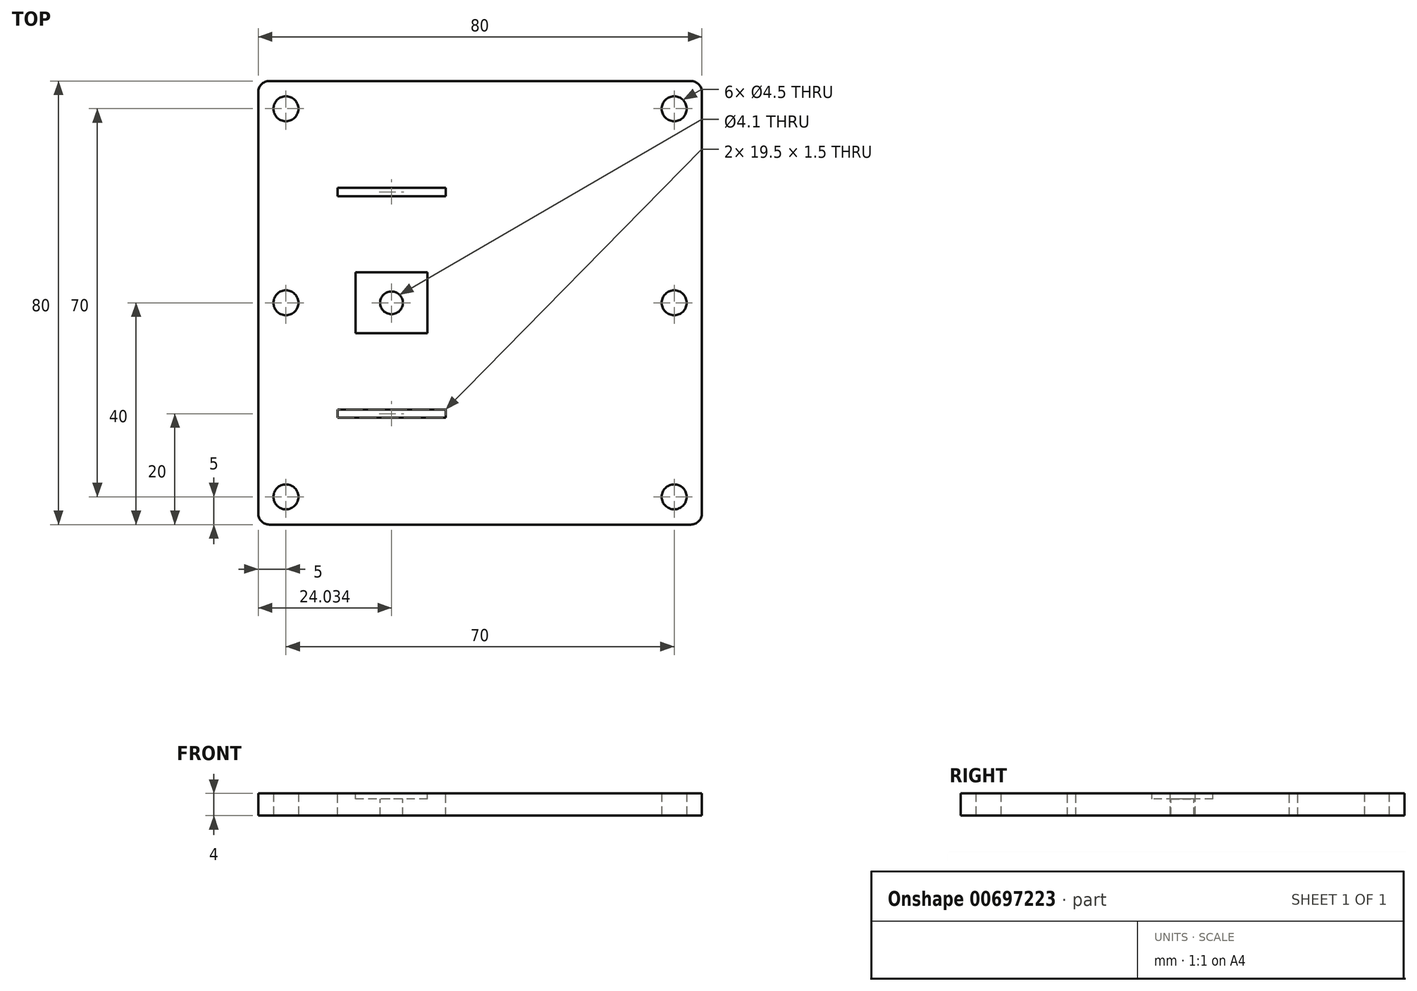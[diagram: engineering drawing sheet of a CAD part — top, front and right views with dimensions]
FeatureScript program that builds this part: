
annotation { "Feature Type Name" : "Feature", "Feature Type Description" : "" }
export const myFeature = defineFeature(function(context is Context, id is Id, definition is map)
    precondition{}
    {
        {
            var Q0;
            Q0=qCreatedBy(makeId("Top.planeOp"),FACE);
            var sketch = newSketch(context, id + "F0", { "sketchPlane" : qUnion([Q0])});
            skLineSegment(sketch, "E0.bottom", {"start": v(38, 40) * mm, "end": v(-38, 40) * mm});
            skLineSegment(sketch, "E0.top", {"start": v(38, -40) * mm, "end": v(-38, -40) * mm});
            skLineSegment(sketch, "E0.left", {"start": v(40, 38) * mm, "end": v(40, -38) * mm});
            skLineSegment(sketch, "E0.right", {"start": v(-40, 38) * mm, "end": v(-40, -38) * mm});
            skPoint(sketch, "E0.middle", {"position": v(0, 0) * mm});
            skCircle(sketch, "E1", {"center": v(-35, 0) * mm, "radius": 2.25 * mm});
            skCircle(sketch, "E2", {"center": v(35, 0) * mm, "radius": 2.25 * mm});
            skPoint(sketch, "E3.visualSharp", {"position": v(-40, 40) * mm});
            skArc(sketch, "E3.filletArc", {"start": v(-38, 40) * mm, "mid": v(-39.41, 39.41) * mm, "end": v(-40, 38) * mm});
            skPoint(sketch, "E4.visualSharp", {"position": v(-40, -40) * mm});
            skArc(sketch, "E4.filletArc", {"start": v(-40, -38) * mm, "mid": v(-39.41, -39.41) * mm, "end": v(-38, -40) * mm});
            skPoint(sketch, "E5.visualSharp", {"position": v(40, 40) * mm});
            skArc(sketch, "E5.filletArc", {"start": v(40, 38) * mm, "mid": v(39.41, 39.41) * mm, "end": v(38, 40) * mm});
            skPoint(sketch, "E6.visualSharp", {"position": v(40, -40) * mm});
            skArc(sketch, "E6.filletArc", {"start": v(38, -40) * mm, "mid": v(39.41, -39.41) * mm, "end": v(40, -38) * mm});
            skLineSegment(sketch, "E7", {"start": v(-35, 0) * mm, "end": v(-35, 40) * mm, "construction": true});
            skLineSegment(sketch, "E8", {"start": v(-35, 0) * mm, "end": v(-35, -40) * mm, "construction": true});
            skLineSegment(sketch, "E9", {"start": v(35, 0) * mm, "end": v(35, 40) * mm, "construction": true});
            skLineSegment(sketch, "E10", {"start": v(35, 0) * mm, "end": v(35, -40) * mm, "construction": true});
            skCircle(sketch, "E11", {"center": v(-35, 35) * mm, "radius": 2.25 * mm});
            skCircle(sketch, "E12", {"center": v(35, 35) * mm, "radius": 2.25 * mm});
            skCircle(sketch, "E13", {"center": v(-35, -35) * mm, "radius": 2.25 * mm});
            skCircle(sketch, "E14", {"center": v(35, -35) * mm, "radius": 2.25 * mm});
            skSolve(sketch);
        }
        {
            var Q0;
            Q0=makeQuery(id+"F0.imprint","IMPRINT",FACE,{"disambiguationData":[TD([[makeQuery(id+"F0.imprint","IMPRINT",EDGE,{"derivedFrom":sQuery(id+"F0.wireOp",EDGE,"E0.bottom")}),1.0]])]});
            extrude(context, id + "F1", {"entities" : qUnion([Q0]), "depth" : 4 * mm, "offsetDistance" : 25 * mm});
        }
        {
            var Q0;
            Q0=makeQuery(id+"F1.opExtrude","CAP_FACE",FACE,{"disambiguationData":[OSD([sQuery(id+"F0.wireOp",EDGE,"E0.bottom"),sQuery(id+"F0.wireOp",EDGE,"E0.top"),sQuery(id+"F0.wireOp",EDGE,"E0.left"),sQuery(id+"F0.wireOp",EDGE,"E0.right"),sQuery(id+"F0.wireOp",EDGE,"E1"),sQuery(id+"F0.wireOp",EDGE,"E2"),sQuery(id+"F0.wireOp",EDGE,"E3.filletArc"),sQuery(id+"F0.wireOp",EDGE,"E4.filletArc"),sQuery(id+"F0.wireOp",EDGE,"E5.filletArc"),sQuery(id+"F0.wireOp",EDGE,"E6.filletArc")])],"isStart":false});
            var sketch = newSketch(context, id + "F2", { "sketchPlane" : qUnion([Q0])});
            skCircle(sketch, "E15", {"center": v(-15.97, 0) * mm, "radius": 2.05 * mm});
            skSolve(sketch);
        }
        {
            var Q0;
            Q0=makeQuery(id+"F2.imprint","IMPRINT",FACE,{"disambiguationData":[TD([[makeQuery(id+"F2.imprint","IMPRINT",EDGE,{"derivedFrom":sQuery(id+"F2.wireOp",EDGE,"E15")}),1.0]])]});
            extrude(context, id + "F3", {"entities" : qUnion([Q0]), "operationType" : NewBodyOperationType.REMOVE, "oppositeDirection" : true, "depth" : 5 * mm, "offsetDistance" : 25 * mm});
        }
        {
            var Q0;
            Q0=makeQuery(id+"F1.opExtrude","CAP_FACE",FACE,{"disambiguationData":[OSD([sQuery(id+"F0.wireOp",EDGE,"E0.bottom"),sQuery(id+"F0.wireOp",EDGE,"E0.top"),sQuery(id+"F0.wireOp",EDGE,"E0.left"),sQuery(id+"F0.wireOp",EDGE,"E0.right"),sQuery(id+"F0.wireOp",EDGE,"E1"),sQuery(id+"F0.wireOp",EDGE,"E2"),sQuery(id+"F0.wireOp",EDGE,"E3.filletArc"),sQuery(id+"F0.wireOp",EDGE,"E4.filletArc"),sQuery(id+"F0.wireOp",EDGE,"E5.filletArc"),sQuery(id+"F0.wireOp",EDGE,"E6.filletArc")])],"isStart":false});
            var sketch = newSketch(context, id + "F4", { "sketchPlane" : qUnion([Q0])});
            skLineSegment(sketch, "E16.bottom", {"start": v(-9.47, 5.5) * mm, "end": v(-22.47, 5.5) * mm});
            skLineSegment(sketch, "E16.top", {"start": v(-9.47, -5.5) * mm, "end": v(-22.47, -5.5) * mm});
            skLineSegment(sketch, "E16.left", {"start": v(-9.47, 5.5) * mm, "end": v(-9.47, -5.5) * mm});
            skLineSegment(sketch, "E16.right", {"start": v(-22.47, 5.5) * mm, "end": v(-22.47, -5.5) * mm});
            skPoint(sketch, "E16.middle", {"position": v(-15.97, 0) * mm});
            skSolve(sketch);
        }
        {
            var Q0;
            Q0=qSketchRegion(id+"F4",true);
            extrude(context, id + "F5", {"entities" : qUnion([Q0]), "operationType" : NewBodyOperationType.REMOVE, "oppositeDirection" : true, "depth" : 1 * mm, "offsetDistance" : 25 * mm});
        }
        {
            var Q0;
            Q0=makeQuery(id+"F1.opExtrude","CAP_FACE",FACE,{"disambiguationData":[OSD([sQuery(id+"F0.wireOp",EDGE,"E0.bottom"),sQuery(id+"F0.wireOp",EDGE,"E0.top"),sQuery(id+"F0.wireOp",EDGE,"E0.left"),sQuery(id+"F0.wireOp",EDGE,"E0.right"),sQuery(id+"F0.wireOp",EDGE,"E1"),sQuery(id+"F0.wireOp",EDGE,"E2"),sQuery(id+"F0.wireOp",EDGE,"E3.filletArc"),sQuery(id+"F0.wireOp",EDGE,"E4.filletArc"),sQuery(id+"F0.wireOp",EDGE,"E5.filletArc"),sQuery(id+"F0.wireOp",EDGE,"E6.filletArc")])],"isStart":false});
            var sketch = newSketch(context, id + "F6", { "sketchPlane" : qUnion([Q0])});
            skCircle(sketch, "E17", {"center": v(-15.97, 0) * mm, "radius": 11.5 * mm});
            skLineSegment(sketch, "E18", {"start": v(-15.97, 5.5) * mm, "end": v(-15.97, -5.5) * mm, "construction": true});
            skLineSegment(sketch, "E19", {"start": v(-22.47, 0) * mm, "end": v(-15.97, 0) * mm, "construction": true});
            skLineSegment(sketch, "E20.bottom", {"start": v(-6.22, -20.75) * mm, "end": v(-25.72, -20.75) * mm});
            skLineSegment(sketch, "E20.top", {"start": v(-6.22, -19.25) * mm, "end": v(-25.72, -19.25) * mm});
            skLineSegment(sketch, "E20.left", {"start": v(-6.22, -20.75) * mm, "end": v(-6.22, -19.25) * mm});
            skLineSegment(sketch, "E20.right", {"start": v(-25.72, -20.75) * mm, "end": v(-25.72, -19.25) * mm});
            skPoint(sketch, "E20.middle", {"position": v(-15.97, -20) * mm});
            skLineSegment(sketch, "E21.bottom", {"start": v(-6.22, 19.25) * mm, "end": v(-25.72, 19.25) * mm});
            skLineSegment(sketch, "E21.top", {"start": v(-6.22, 20.75) * mm, "end": v(-25.72, 20.75) * mm});
            skLineSegment(sketch, "E21.left", {"start": v(-6.22, 19.25) * mm, "end": v(-6.22, 20.75) * mm});
            skLineSegment(sketch, "E21.right", {"start": v(-25.72, 19.25) * mm, "end": v(-25.72, 20.75) * mm});
            skPoint(sketch, "E21.middle", {"position": v(-15.97, 20) * mm});
            skSolve(sketch);
        }
        {
            var Q0;
            Q0=makeQuery(id+"F6.imprint","IMPRINT",FACE,{"disambiguationData":[TD([[makeQuery(id+"F6.imprint","IMPRINT",EDGE,{"derivedFrom":sQuery(id+"F6.wireOp",EDGE,"4c36ce2d-7893-4952-8c75-719a712cee38.bottom")}),-1.0]])]});
            var Q1;
            Q1=makeQuery(id+"F6.imprint","IMPRINT",FACE,{"disambiguationData":[TD([[makeQuery(id+"F6.imprint","IMPRINT",EDGE,{"derivedFrom":sQuery(id+"F6.wireOp",EDGE,"4ac7b2f1-0ae4-4ee0-8eeb-5f562c3d152a.bottom")}),-1.0]])]});
            var Q2;
            Q2=makeQuery(id+"F6.imprint","IMPRINT",FACE,{"disambiguationData":[TD([[makeQuery(id+"F6.imprint","IMPRINT",EDGE,{"derivedFrom":sQuery(id+"F6.wireOp",EDGE,"E21.bottom")}),-1.0]])]});
            var Q3;
            Q3=makeQuery(id+"F6.imprint","IMPRINT",FACE,{"disambiguationData":[TD([[makeQuery(id+"F6.imprint","IMPRINT",EDGE,{"derivedFrom":sQuery(id+"F6.wireOp",EDGE,"E20.bottom")}),-1.0]])]});
            extrude(context, id + "F7", {"entities" : qUnion([Q0, Q1, Q2, Q3]), "operationType" : NewBodyOperationType.REMOVE, "oppositeDirection" : true, "depth" : 25 * mm, "offsetDistance" : 25 * mm});
        }
    });
